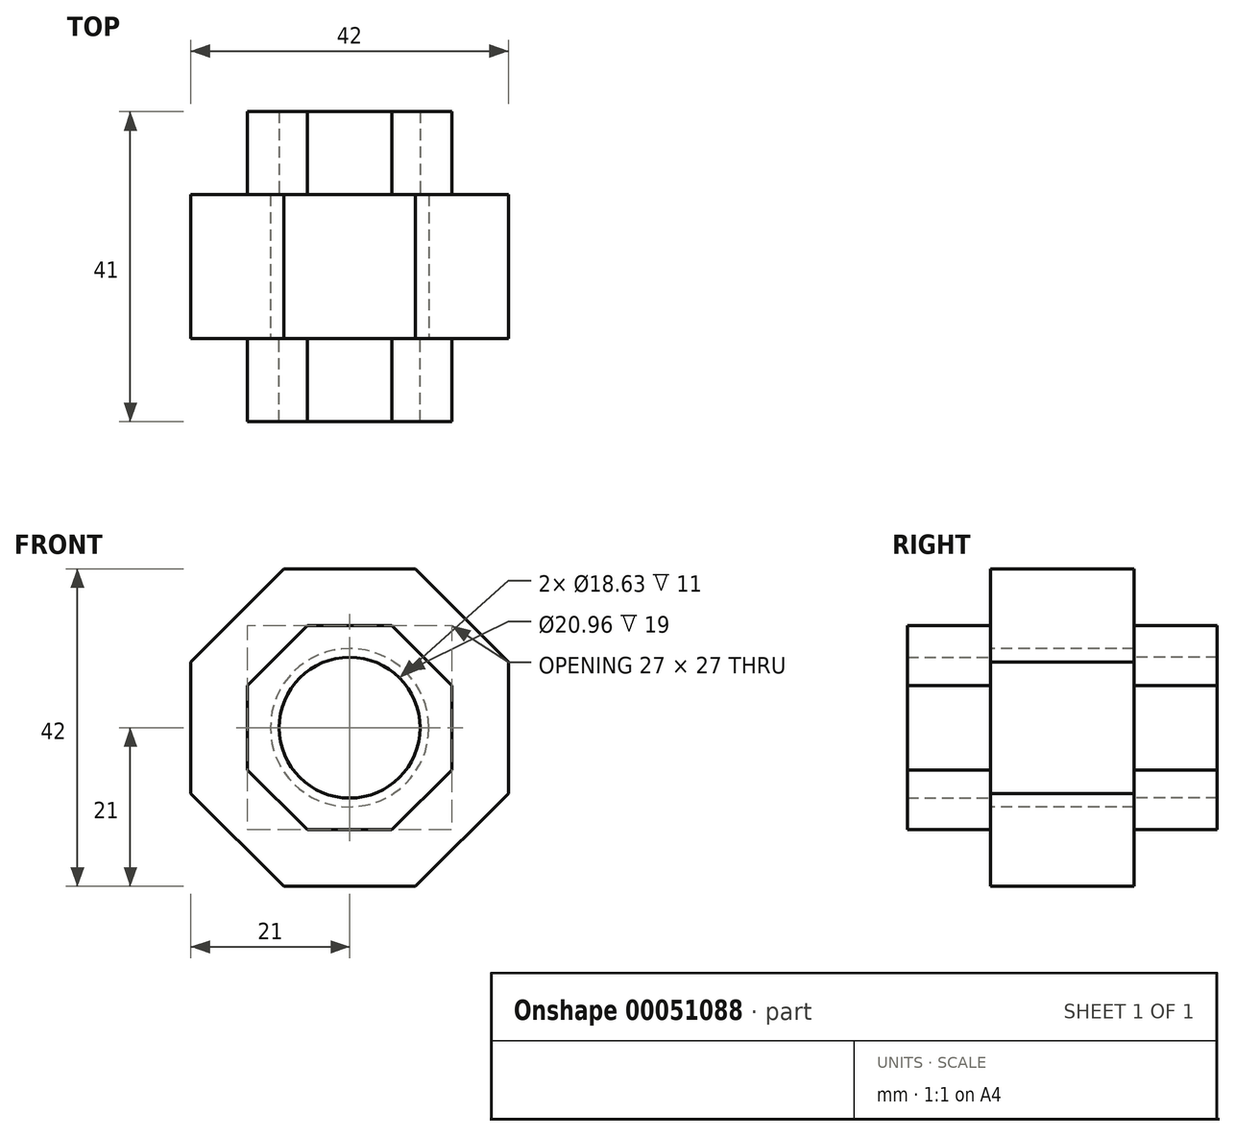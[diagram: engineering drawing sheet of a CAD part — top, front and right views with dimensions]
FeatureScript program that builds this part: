
annotation { "Feature Type Name" : "Feature", "Feature Type Description" : "" }
export const myFeature = defineFeature(function(context is Context, id is Id, definition is map)
    precondition{}
    {
        {
            var Q0;
            Q0=qCreatedBy(makeId("Front.planeOp"),FACE);
            var sketch = newSketch(context, id + "F0", { "sketchPlane" : qUnion([Q0])});
            skCircle(sketch, "E0", {"center": v(0, 0) * mm, "radius": 9.32 * mm});
            skCircle(sketch, "E1.cCircle", {"center": v(0, 0) * mm, "radius": 13.5 * mm, "construction": true});
            skLineSegment(sketch, "E1.0", {"start": v(13.5, 5.6) * mm, "end": v(13.5, -5.6) * mm});
            skLineSegment(sketch, "E1.1", {"start": v(13.5, -5.6) * mm, "end": v(5.6, -13.5) * mm});
            skLineSegment(sketch, "E1.2", {"start": v(5.6, -13.5) * mm, "end": v(-5.6, -13.5) * mm});
            skLineSegment(sketch, "E1.3", {"start": v(-5.6, -13.5) * mm, "end": v(-13.5, -5.6) * mm});
            skLineSegment(sketch, "E1.4", {"start": v(-13.5, -5.6) * mm, "end": v(-13.5, 5.6) * mm});
            skLineSegment(sketch, "E1.5", {"start": v(-13.5, 5.6) * mm, "end": v(-5.6, 13.5) * mm});
            skLineSegment(sketch, "E1.6", {"start": v(-5.6, 13.5) * mm, "end": v(5.6, 13.5) * mm});
            skLineSegment(sketch, "E1.7", {"start": v(5.6, 13.5) * mm, "end": v(13.5, 5.6) * mm});
            skPoint(sketch, "E1.0.midPoint", {"position": v(13.5, 0) * mm});
            skSolve(sketch);
        }
        {
            var Q0;
            Q0=qSketchRegion(id+"F0",true);
            extrude(context, id + "F1", {"entities" : qUnion([Q0]), "depth" : 11 * mm});
        }
        {
            var Q0;
            Q0=makeQuery(id+"F1.opExtrude","CAP_FACE",FACE,{"disambiguationData":[OSD([sQuery(id+"F0.wireOp",EDGE,"E0"),sQuery(id+"F0.wireOp",EDGE,"E1.0"),sQuery(id+"F0.wireOp",EDGE,"E1.1"),sQuery(id+"F0.wireOp",EDGE,"E1.2"),sQuery(id+"F0.wireOp",EDGE,"E1.3"),sQuery(id+"F0.wireOp",EDGE,"E1.4"),sQuery(id+"F0.wireOp",EDGE,"E1.5"),sQuery(id+"F0.wireOp",EDGE,"E1.6"),sQuery(id+"F0.wireOp",EDGE,"E1.7")])],"isStart":true});
            var sketch = newSketch(context, id + "F2", { "sketchPlane" : qUnion([Q0])});
            skCircle(sketch, "E2", {"center": v(0, 0) * mm, "radius": 10.48 * mm});
            skCircle(sketch, "E3.cCircle", {"center": v(0, 0) * mm, "radius": 21 * mm, "construction": true});
            skPoint(sketch, "E3.cCircle.perimeterSnap0", {"position": v(13.5, 0) * mm});
            skLineSegment(sketch, "E3.0", {"start": v(21, 8.7) * mm, "end": v(21, -8.7) * mm});
            skLineSegment(sketch, "E3.1", {"start": v(21, -8.7) * mm, "end": v(8.7, -21) * mm});
            skLineSegment(sketch, "E3.2", {"start": v(8.7, -21) * mm, "end": v(-8.7, -21) * mm});
            skLineSegment(sketch, "E3.3", {"start": v(-8.7, -21) * mm, "end": v(-21, -8.7) * mm});
            skLineSegment(sketch, "E3.4", {"start": v(-21, -8.7) * mm, "end": v(-21, 8.7) * mm});
            skLineSegment(sketch, "E3.5", {"start": v(-21, 8.7) * mm, "end": v(-8.7, 21) * mm});
            skLineSegment(sketch, "E3.6", {"start": v(-8.7, 21) * mm, "end": v(8.7, 21) * mm});
            skLineSegment(sketch, "E3.7", {"start": v(8.7, 21) * mm, "end": v(21, 8.7) * mm});
            skPoint(sketch, "E3.0.midPoint", {"position": v(21, 0) * mm});
            skPoint(sketch, "E3.0.midPoint.positionSnap0", {"position": v(13.5, 0) * mm});
            skSolve(sketch);
        }
        {
            var Q0;
            Q0=qSketchRegion(id+"F2",true);
            extrude(context, id + "F3", {"entities" : qUnion([Q0]), "operationType" : NewBodyOperationType.ADD, "depth" : (41 - 22) * mm});
        }
        {
            var Q0;
            Q0=makeQuery(id+"F3.opExtrude","CAP_FACE",FACE,{"disambiguationData":[OSD([sQuery(id+"F2.wireOp",EDGE,"E2"),sQuery(id+"F2.wireOp",EDGE,"E3.0"),sQuery(id+"F2.wireOp",EDGE,"E3.1"),sQuery(id+"F2.wireOp",EDGE,"E3.2"),sQuery(id+"F2.wireOp",EDGE,"E3.3"),sQuery(id+"F2.wireOp",EDGE,"E3.4"),sQuery(id+"F2.wireOp",EDGE,"E3.5"),sQuery(id+"F2.wireOp",EDGE,"E3.6"),sQuery(id+"F2.wireOp",EDGE,"E3.7")])],"isStart":false});
            var sketch = newSketch(context, id + "F4", { "sketchPlane" : qUnion([Q0])});
            skCircle(sketch, "E4", {"center": v(0, 0) * mm, "radius": 9.32 * mm});
            skCircle(sketch, "E5.cCircle", {"center": v(0, 0) * mm, "radius": 13.5 * mm, "construction": true});
            skLineSegment(sketch, "E5.0", {"start": v(13.5, 5.6) * mm, "end": v(13.5, -5.6) * mm});
            skLineSegment(sketch, "E5.1", {"start": v(13.5, -5.6) * mm, "end": v(5.6, -13.5) * mm});
            skLineSegment(sketch, "E5.2", {"start": v(5.6, -13.5) * mm, "end": v(-5.6, -13.5) * mm});
            skLineSegment(sketch, "E5.3", {"start": v(-5.6, -13.5) * mm, "end": v(-13.5, -5.6) * mm});
            skLineSegment(sketch, "E5.4", {"start": v(-13.5, -5.6) * mm, "end": v(-13.5, 5.6) * mm});
            skLineSegment(sketch, "E5.5", {"start": v(-13.5, 5.6) * mm, "end": v(-5.6, 13.5) * mm});
            skLineSegment(sketch, "E5.6", {"start": v(-5.6, 13.5) * mm, "end": v(5.6, 13.5) * mm});
            skLineSegment(sketch, "E5.7", {"start": v(5.6, 13.5) * mm, "end": v(13.5, 5.6) * mm});
            skPoint(sketch, "E5.0.midPoint", {"position": v(13.5, 0) * mm});
            skSolve(sketch);
        }
        {
            var Q0;
            Q0=qSketchRegion(id+"F4",true);
            extrude(context, id + "F5", {"entities" : qUnion([Q0]), "operationType" : NewBodyOperationType.ADD, "depth" : 11 * mm});
        }
    });
